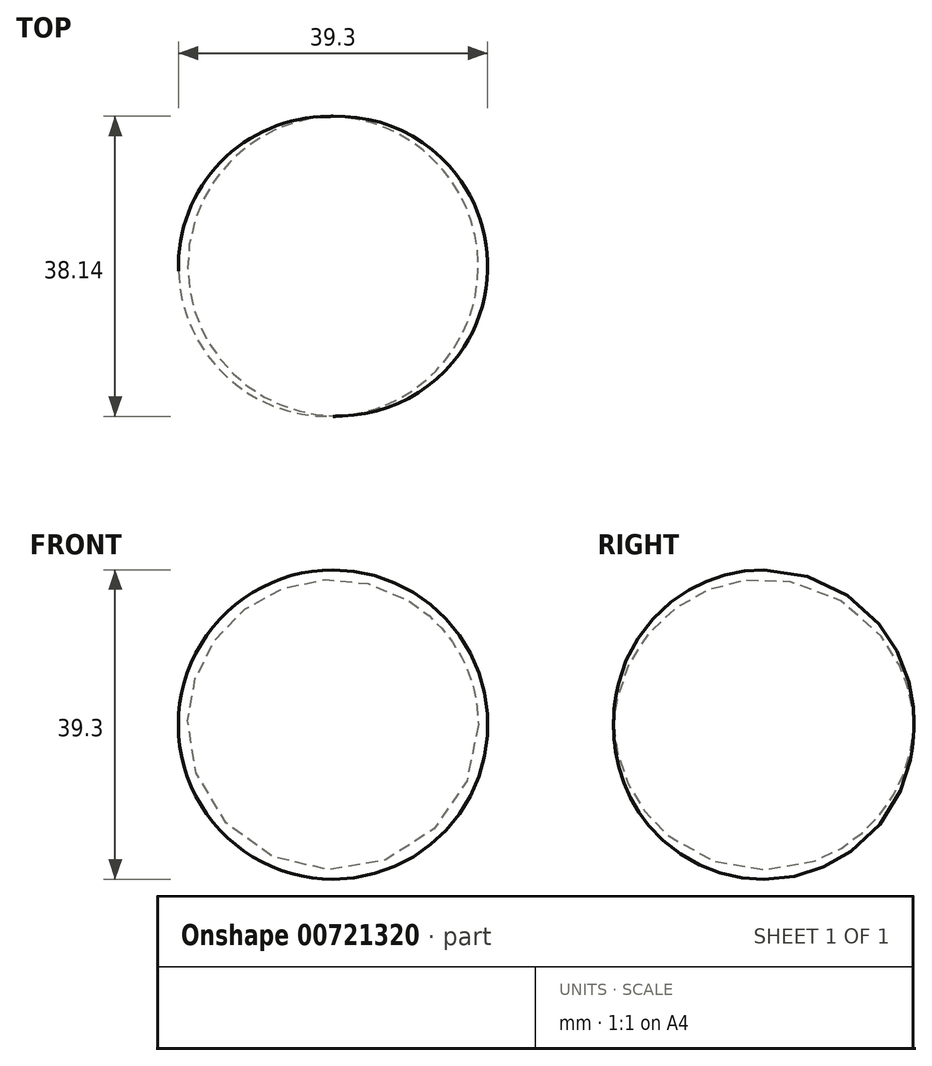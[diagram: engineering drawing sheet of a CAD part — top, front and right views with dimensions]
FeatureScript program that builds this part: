
annotation { "Feature Type Name" : "Feature", "Feature Type Description" : "" }
export const myFeature = defineFeature(function(context is Context, id is Id, definition is map)
    precondition{}
    {
        {
            var Q0;
            Q0=qCreatedBy(makeId("Top.planeOp"),FACE);
            var sketch = newSketch(context, id + "F0", { "sketchPlane" : qUnion([Q0])});
            skArc(sketch, "E0", {"start": v(-1.2, 19.01) * mm, "mid": v(-19.04, -0.6) * mm, "end": v(0, -19.05) * mm});
            skLineSegment(sketch, "E1", {"start": v(-1.2, 19.01) * mm, "end": v(0, -19.05) * mm});
            skSolve(sketch);
        }
        {
            var Q0;
            Q0=makeQuery(id+"F0.imprint","IMPRINT",FACE,{"disambiguationData":[TD([[makeQuery(id+"F0.imprint","IMPRINT",EDGE,{"derivedFrom":sQuery(id+"F0.wireOp",EDGE,"E0")}),1.0]])]});
            var Q1;
            Q1=sQuery(id+"F0.wireOp",EDGE,"E1");
            revolve(context, id + "F1", {"surfaceOperationType" : NewSurfaceOperationType.NEW, "entities" : qUnion([Q0]), "axis" : qUnion([Q1]), "revolveType" : RevolveType.FULL});
        }
    });
